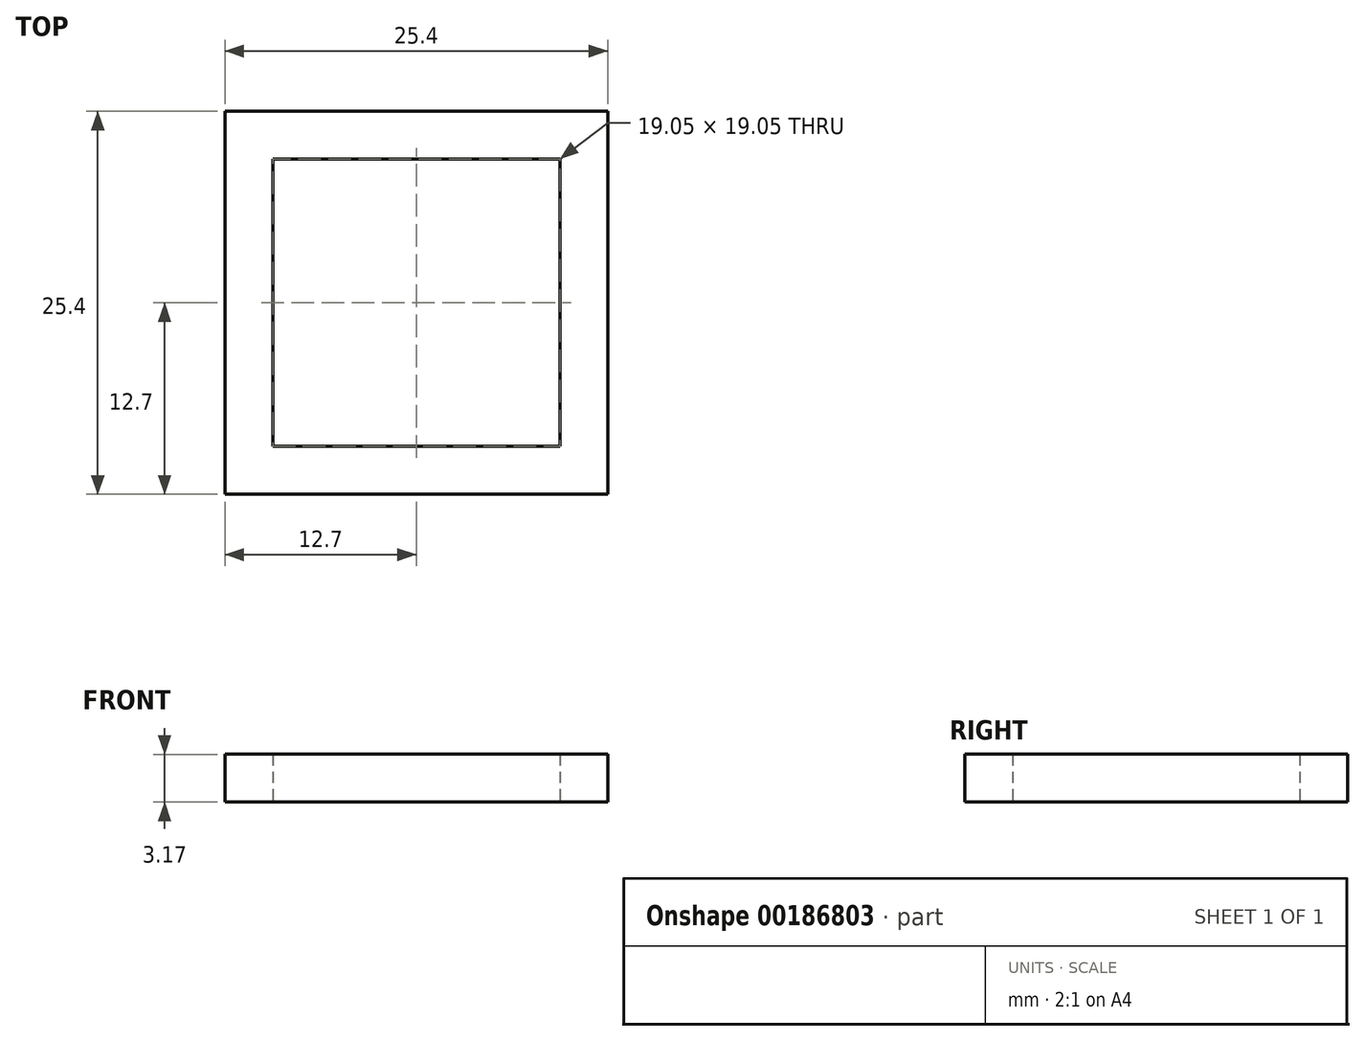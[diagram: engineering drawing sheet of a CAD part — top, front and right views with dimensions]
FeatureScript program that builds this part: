
annotation { "Feature Type Name" : "Feature", "Feature Type Description" : "" }
export const myFeature = defineFeature(function(context is Context, id is Id, definition is map)
    precondition{}
    {
        {
            var Q0;
            Q0=qCreatedBy(makeId("Top.planeOp"),FACE);
            var sketch = newSketch(context, id + "F0", { "sketchPlane" : qUnion([Q0])});
            skLineSegment(sketch, "E0.bottom", {"start": v(-12.7, 12.7) * mm, "end": v(12.7, 12.7) * mm});
            skLineSegment(sketch, "E0.top", {"start": v(-12.7, -12.7) * mm, "end": v(12.7, -12.7) * mm});
            skLineSegment(sketch, "E0.left", {"start": v(-12.7, 12.7) * mm, "end": v(-12.7, -12.7) * mm});
            skLineSegment(sketch, "E0.right", {"start": v(12.7, 12.7) * mm, "end": v(12.7, -12.7) * mm});
            skLineSegment(sketch, "E1.bottom", {"start": v(-9.53, 9.52) * mm, "end": v(9.53, 9.52) * mm});
            skLineSegment(sketch, "E1.top", {"start": v(-9.53, -9.53) * mm, "end": v(9.53, -9.53) * mm});
            skLineSegment(sketch, "E1.left", {"start": v(-9.53, 9.52) * mm, "end": v(-9.53, -9.53) * mm});
            skLineSegment(sketch, "E1.right", {"start": v(9.53, 9.52) * mm, "end": v(9.53, -9.53) * mm});
            skSolve(sketch);
        }
        {
            var Q0;
            Q0 = qSketchRegion(id + "F0", true);
            extrude(context, id + "F1", {"entities" : qUnion([Q0]), "depth" : 3.17 * mm});
        }
    });
